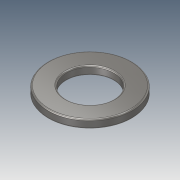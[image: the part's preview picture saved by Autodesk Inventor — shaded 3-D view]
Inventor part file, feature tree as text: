
AUTODESK INVENTOR PART (.ipt)
format: ipt  version: 2018.2 (Build 222227000, 227)  size: 121,344 bytes
history: native  units: mm
features: extrude x1, fillet x1, sketch x1
ambient origin geometry x8: Origin, YZ Plane, XZ Plane, XY Plane, X Axis, Y Axis, Z Axis, Center Point
bodies: Volumenkörper1 (feature_tree)
feature tree (3):
  extrude  "Extrusion1"  Depth=0.25mm
  fillet  "Rundung1"  Radius=1.6mm
  sketch  "Skizze1"  dims[d0=9.0mm d1=16.0mm d2=1.6mm d3=0.0mm d4=0.25mm]
